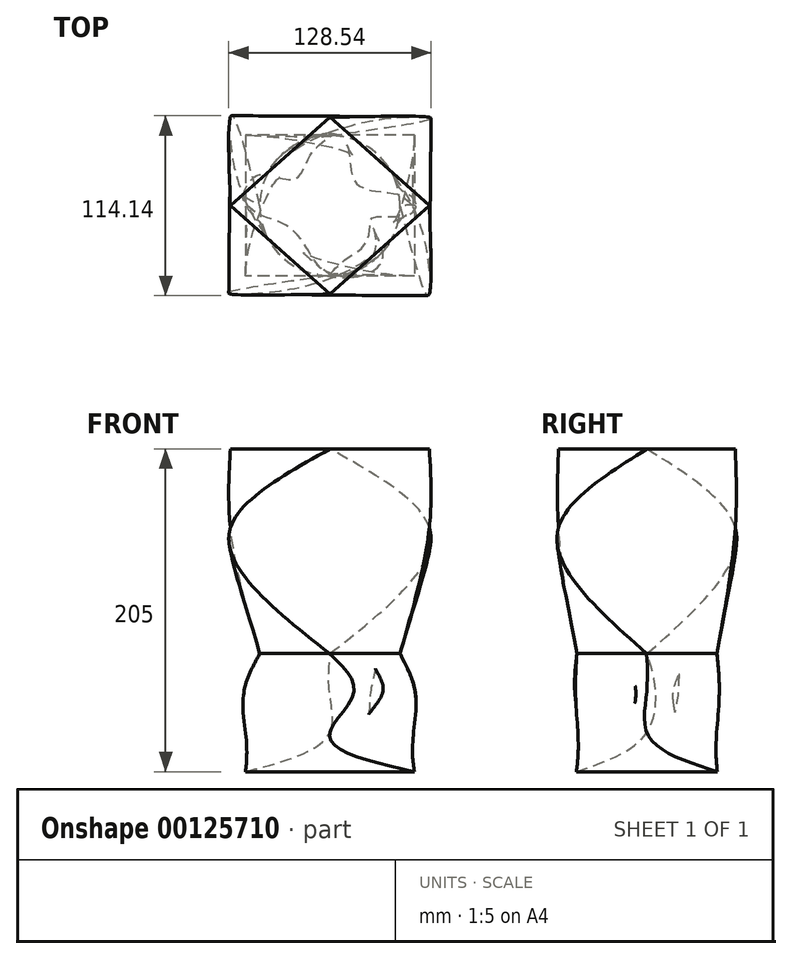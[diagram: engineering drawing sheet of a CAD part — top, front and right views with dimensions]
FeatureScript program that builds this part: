
annotation { "Feature Type Name" : "Feature", "Feature Type Description" : "" }
export const myFeature = defineFeature(function(context is Context, id is Id, definition is map)
    precondition{}
    {
        {
            var Q0;
            Q0=qCreatedBy(makeId("Top.planeOp"),FACE);
            cPlane(context, id + "F0", {"entities" : qUnion([Q0]), "cplaneType" : CPlaneType.OFFSET, "offset" : 25 * mm, "width" : 152.4 * mm, "height" : 152.4 * mm});
        }
        {
            var Q0;
            Q0=qCreatedBy(id+"F0.planeOp",FACE);
            cPlane(context, id + "F1", {"entities" : qUnion([Q0]), "cplaneType" : CPlaneType.OFFSET, "offset" : 25 * mm, "width" : 150 * mm, "height" : 150 * mm});
        }
        {
            var Q0;
            Q0=qCreatedBy(id+"F1.planeOp",FACE);
            cPlane(context, id + "F2", {"entities" : qUnion([Q0]), "cplaneType" : CPlaneType.OFFSET, "offset" : 25 * mm, "width" : 150 * mm, "height" : 150 * mm});
        }
        {
            var Q0;
            Q0=qCreatedBy(makeId("Top.planeOp"),FACE);
            var sketch = newSketch(context, id + "F3", { "sketchPlane" : qUnion([Q0])});
            skLineSegment(sketch, "E0.bottom", {"start": v(53.61, 44.75) * mm, "end": v(-53.61, 44.75) * mm});
            skLineSegment(sketch, "E0.top", {"start": v(53.61, -44.75) * mm, "end": v(-53.61, -44.75) * mm});
            skLineSegment(sketch, "E0.left", {"start": v(53.61, 44.75) * mm, "end": v(53.61, -44.75) * mm});
            skLineSegment(sketch, "E0.right", {"start": v(-53.61, 44.75) * mm, "end": v(-53.61, -44.75) * mm});
            skPoint(sketch, "E0.middle", {"position": v(0, 0) * mm});
            skSolve(sketch);
        }
        {
            var Q0;
            Q0=qCreatedBy(id+"F0.planeOp",FACE);
            var sketch = newSketch(context, id + "F4", { "sketchPlane" : qUnion([Q0])});
            skLineSegment(sketch, "E1", {"start": v(-53.61, 0) * mm, "end": v(0, 44.3) * mm});
            skLineSegment(sketch, "E2", {"start": v(0, 44.3) * mm, "end": v(53.16, 0) * mm});
            skLineSegment(sketch, "E3", {"start": v(-53.61, 0) * mm, "end": v(0, -43.84) * mm});
            skLineSegment(sketch, "E4", {"start": v(0, -43.84) * mm, "end": v(53.16, 0) * mm});
            skSolve(sketch);
        }
        {
            var Q0;
            Q0=qCreatedBy(id+"F1.planeOp",FACE);
            var sketch = newSketch(context, id + "F5", { "sketchPlane" : qUnion([Q0])});
            skFitSpline(sketch, "E5", {"points": [v(0, -43.84) * mm, v(33.17, -33.4) * mm, v(26.35, -8.4) * mm, v(49.98, -5.68) * mm, v(52.25, 5.22) * mm, v(17.72, 13.4) * mm, v(10, 40.2) * mm, v(-7.72, 43.39) * mm, v(-21.8, 17.5) * mm, v(-45.43, 19.3) * mm, v(-53.61, 0) * mm, v(-24.08, -15.22) * mm, v(0, -43.84) * mm]});
            skSolve(sketch);
        }
        {
            var Q0;
            Q0=qCreatedBy(id+"F2.planeOp",FACE);
            var sketch = newSketch(context, id + "F6", { "sketchPlane" : qUnion([Q0])});
            skCircle(sketch, "E6", {"center": v(0, 0) * mm, "radius": 44.53 * mm});
            skSolve(sketch);
        }
        {
            var Q0;
            Q0=makeQuery(id+"F3.imprint","IMPRINT",FACE,{"disambiguationData":[TD([[makeQuery(id+"F3.imprint","IMPRINT",EDGE,{"derivedFrom":sQuery(id+"F3.wireOp",EDGE,"E0.bottom")}),1.0]])]});
            var Q1;
            Q1=makeQuery(id+"F4.imprint","IMPRINT",FACE,{"disambiguationData":[TD([[makeQuery(id+"F4.imprint","IMPRINT",EDGE,{"derivedFrom":sQuery(id+"F4.wireOp",EDGE,"E1")}),-1.0]])]});
            var Q2;
            Q2=makeQuery(id+"F5.imprint","IMPRINT",FACE,{"disambiguationData":[TD([[makeQuery(id+"F5.imprint","IMPRINT",EDGE,{"derivedFrom":sQuery(id+"F5.wireOp",EDGE,"E5")}),1.0]])]});
            var Q3;
            Q3=makeQuery(id+"F6.imprint","IMPRINT",FACE,{"disambiguationData":[TD([[makeQuery(id+"F6.imprint","IMPRINT",EDGE,{"derivedFrom":sQuery(id+"F6.wireOp",EDGE,"E6")}),1.0]])]});
            loft(context, id + "F7", {"sheetProfilesArray" : [{ "sheetProfileEntities" : qUnion([Q0]) }, { "sheetProfileEntities" : qUnion([Q1]) }, { "sheetProfileEntities" : qUnion([Q2]) }, { "sheetProfileEntities" : qUnion([Q3]) }]});
        }
        {
            var Q0;
            Q0=qCreatedBy(id+"F2.planeOp",FACE);
            cPlane(context, id + "F8", {"entities" : qUnion([Q0]), "cplaneType" : CPlaneType.OFFSET, "offset" : 80 * mm, "width" : 150 * mm, "height" : 150 * mm});
        }
        {
            var Q0;
            Q0=qCreatedBy(id+"F8.planeOp",FACE);
            cPlane(context, id + "F9", {"entities" : qUnion([Q0]), "cplaneType" : CPlaneType.OFFSET, "offset" : 50 * mm, "width" : 150 * mm, "height" : 150 * mm});
        }
        {
            var Q0;
            Q0=qCreatedBy(id+"F8.planeOp",FACE);
            var sketch = newSketch(context, id + "F10", { "sketchPlane" : qUnion([Q0])});
            skLineSegment(sketch, "E7.bottom", {"start": v(-63.15, 56.14) * mm, "end": v(63.15, 56.14) * mm});
            skLineSegment(sketch, "E7.top", {"start": v(-63.15, -56.14) * mm, "end": v(63.15, -56.14) * mm});
            skLineSegment(sketch, "E7.left", {"start": v(-63.15, 56.14) * mm, "end": v(-63.15, -56.14) * mm});
            skLineSegment(sketch, "E7.right", {"start": v(63.15, 56.14) * mm, "end": v(63.15, -56.14) * mm});
            skPoint(sketch, "E7.middle", {"position": v(0, 0) * mm});
            skSolve(sketch);
        }
        {
            var Q0;
            Q0=qCreatedBy(id+"F9.planeOp",FACE);
            var sketch = newSketch(context, id + "F11", { "sketchPlane" : qUnion([Q0])});
            skLineSegment(sketch, "E8", {"start": v(-63.15, 0) * mm, "end": v(0, -56.14) * mm});
            skLineSegment(sketch, "E9", {"start": v(0, -56.14) * mm, "end": v(63.15, 0) * mm});
            skLineSegment(sketch, "E10", {"start": v(63.15, 0) * mm, "end": v(0, 56.14) * mm});
            skLineSegment(sketch, "E11", {"start": v(0, 56.14) * mm, "end": v(-63.15, 0) * mm});
            skSolve(sketch);
        }
        {
            var Q1;
            Q1=makeQuery(id+"F7.opLoft","CAP_FACE",FACE,{"disambiguationData":[OSD([makeQuery(id+"F6.imprint","IMPRINT",FACE,{"disambiguationData":[TD([[makeQuery(id+"F6.imprint","IMPRINT",EDGE,{"derivedFrom":sQuery(id+"F6.wireOp",EDGE,"E6")}),1.0]])]})])],"isStart":true});
            var Q2;
            Q2=makeQuery(id+"F10.imprint","IMPRINT",FACE,{"disambiguationData":[TD([[makeQuery(id+"F10.imprint","IMPRINT",EDGE,{"derivedFrom":sQuery(id+"F10.wireOp",EDGE,"E7.bottom")}),-1.0]])]});
            var Q3;
            Q3=makeQuery(id+"F11.imprint","IMPRINT",FACE,{"disambiguationData":[TD([[makeQuery(id+"F11.imprint","IMPRINT",EDGE,{"derivedFrom":sQuery(id+"F11.wireOp",EDGE,"E8")}),1.0]])]});
            loft(context, id + "F12", {"operationType" : NewBodyOperationType.ADD, "sheetProfilesArray" : [{ "sheetProfileEntities" : qUnion([Q1]) }, { "sheetProfileEntities" : qUnion([Q2]) }, { "sheetProfileEntities" : qUnion([Q3]) }]});
        }
    });
